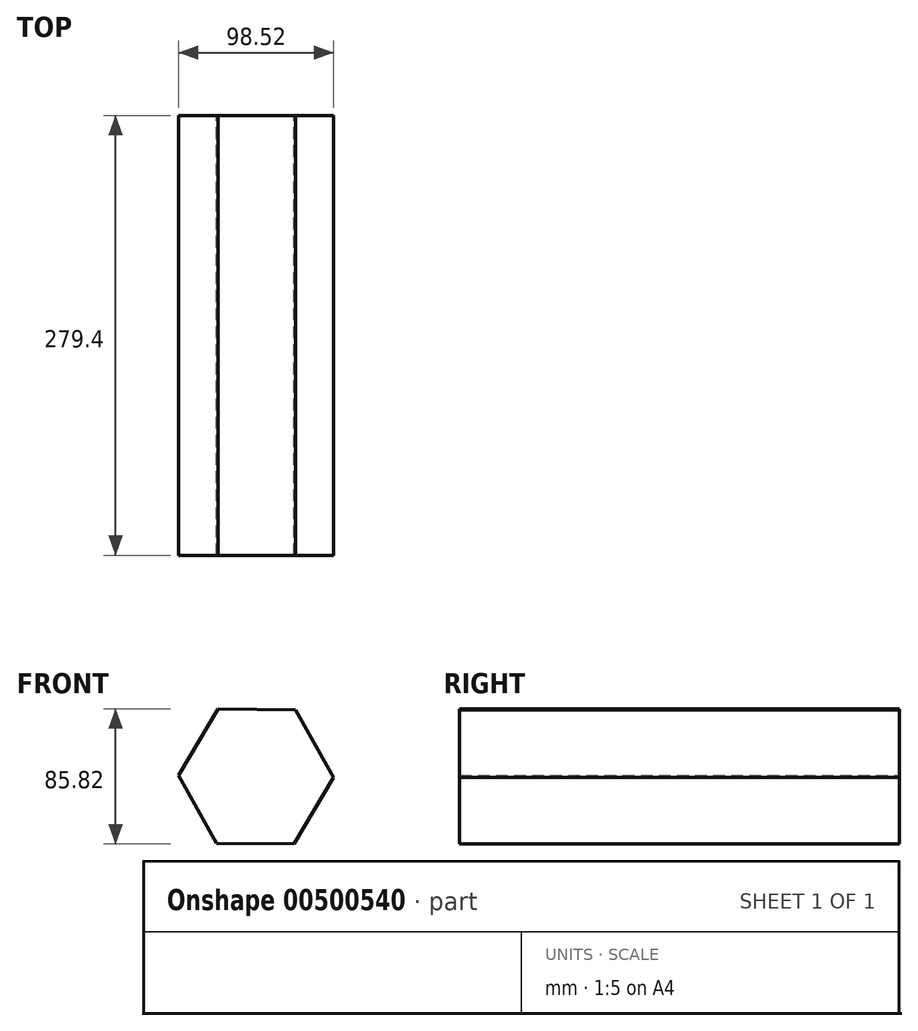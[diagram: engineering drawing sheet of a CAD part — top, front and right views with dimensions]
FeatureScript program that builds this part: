
annotation { "Feature Type Name" : "Feature", "Feature Type Description" : "" }
export const myFeature = defineFeature(function(context is Context, id is Id, definition is map)
    precondition{}
    {
        {
            var Q0;
            Q0=qCreatedBy(makeId("Front.planeOp"),FACE);
            var sketch = newSketch(context, id + "F0", { "sketchPlane" : qUnion([Q0])});
            skCircle(sketch, "E0.cCircle", {"center": v(0, 0) * mm, "radius": 49.26 * mm, "construction": true});
            skLineSegment(sketch, "E0.0", {"start": v(25.07, 42.4) * mm, "end": v(49.26, -0.5) * mm});
            skLineSegment(sketch, "E0.1", {"start": v(49.26, -0.5) * mm, "end": v(24.2, -42.91) * mm});
            skLineSegment(sketch, "E0.2", {"start": v(24.2, -42.91) * mm, "end": v(-25.07, -42.4) * mm});
            skLineSegment(sketch, "E0.3", {"start": v(-25.07, -42.4) * mm, "end": v(-49.26, 0.5) * mm});
            skLineSegment(sketch, "E0.4", {"start": v(-49.26, 0.5) * mm, "end": v(-24.2, 42.91) * mm});
            skLineSegment(sketch, "E0.5", {"start": v(-24.2, 42.91) * mm, "end": v(25.07, 42.4) * mm});
            skSolve(sketch);
        }
        {
            var Q0;
            Q0=makeQuery(id+"F0.imprint","IMPRINT",FACE,{"disambiguationData":[TD([[makeQuery(id+"F0.imprint","IMPRINT",EDGE,{"derivedFrom":sQuery(id+"F0.wireOp",EDGE,"E0.0")}),-1.0]])]});
            extrude(context, id + "F1", {"entities" : qUnion([Q0]), "depth" : 279.4 * mm});
        }
    });
